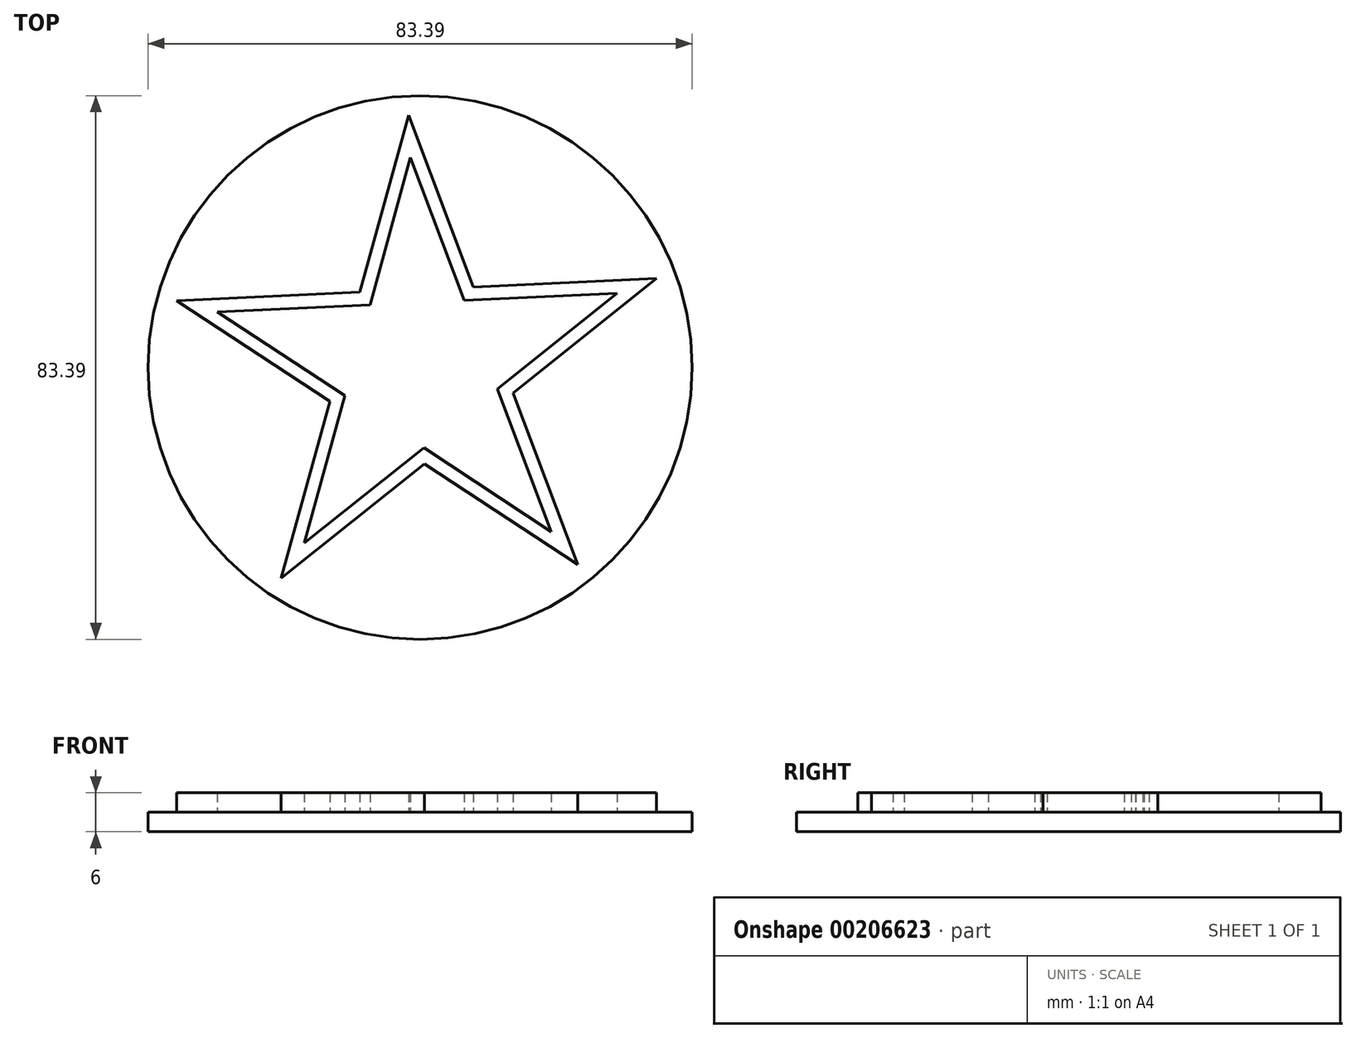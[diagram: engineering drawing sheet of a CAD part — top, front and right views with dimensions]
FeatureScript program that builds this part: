
annotation { "Feature Type Name" : "Feature", "Feature Type Description" : "" }
export const myFeature = defineFeature(function(context is Context, id is Id, definition is map)
    precondition{}
    {
        {
            var Q0;
            Q0=qCreatedBy(makeId("Top.planeOp"),FACE);
            var sketch = newSketch(context, id + "F0", { "sketchPlane" : qUnion([Q0])});
            skLineSegment(sketch, "E0", {"start": v(-46.48, 17.77) * mm, "end": v(-18.4, 19.06) * mm});
            skLineSegment(sketch, "E1", {"start": v(-18.4, 19.06) * mm, "end": v(-10.94, 46.17) * mm});
            skLineSegment(sketch, "E2", {"start": v(-10.94, 46.17) * mm, "end": v(-1.04, 19.86) * mm});
            skLineSegment(sketch, "E3", {"start": v(-1.04, 19.86) * mm, "end": v(27.05, 21.15) * mm});
            skLineSegment(sketch, "E4", {"start": v(27.05, 21.15) * mm, "end": v(5.08, 3.6) * mm});
            skLineSegment(sketch, "E5", {"start": v(5.08, 3.6) * mm, "end": v(15, -22.71) * mm});
            skLineSegment(sketch, "E6", {"start": v(15, -22.71) * mm, "end": v(-8.49, -7.25) * mm});
            skLineSegment(sketch, "E7", {"start": v(-8.49, -7.25) * mm, "end": v(-30.45, -24.8) * mm});
            skLineSegment(sketch, "E8", {"start": v(-30.45, -24.8) * mm, "end": v(-23, 2.3) * mm});
            skLineSegment(sketch, "E9", {"start": v(-23, 2.3) * mm, "end": v(-46.48, 17.77) * mm});
            skLineSegment(sketch, "E10.0", {"start": v(-7.39, -5.58) * mm, "end": v(-8.6, -4.78) * mm});
            skLineSegment(sketch, "E11.0", {"start": v(-21.07, 1.78) * mm, "end": v(-20.69, 3.18) * mm});
            skLineSegment(sketch, "E12.0", {"start": v(-0.95, 17.86) * mm, "end": v(20.99, 18.87) * mm});
            skLineSegment(sketch, "E13.0", {"start": v(3.21, 2.9) * mm, "end": v(10.95, -17.66) * mm});
            skLineSegment(sketch, "E14.0", {"start": v(-9.74, -5.69) * mm, "end": v(-26.9, -19.4) * mm});
            skLineSegment(sketch, "E15.trimOffspring", {"start": v(-10.65, 39.7) * mm, "end": v(-2.4, 17.8) * mm});
            skLineSegment(sketch, "E16.trimOffspring", {"start": v(20.99, 18.87) * mm, "end": v(2.7, 4.25) * mm});
            skLineSegment(sketch, "E17.trimOffspring", {"start": v(10.95, -17.66) * mm, "end": v(-7.39, -5.58) * mm});
            skLineSegment(sketch, "E18.trimOffspring", {"start": v(-26.9, -19.4) * mm, "end": v(-21.07, 1.78) * mm});
            skLineSegment(sketch, "E19.trimOffspring", {"start": v(-40.24, 16.06) * mm, "end": v(-16.85, 17.13) * mm});
            skLineSegment(sketch, "E20.trimOffspring", {"start": v(-2.4, 17.8) * mm, "end": v(-0.95, 17.86) * mm});
            skLineSegment(sketch, "E21.trimOffspring", {"start": v(2.7, 4.25) * mm, "end": v(3.21, 2.9) * mm});
            skLineSegment(sketch, "E22.trimOffspring", {"start": v(-8.6, -4.78) * mm, "end": v(-9.74, -5.69) * mm});
            skLineSegment(sketch, "E23.trimOffspring", {"start": v(-20.69, 3.18) * mm, "end": v(-40.24, 16.06) * mm});
            skLineSegment(sketch, "E24.trimOffspring", {"start": v(-16.85, 17.13) * mm, "end": v(-10.65, 39.7) * mm});
            skCircle(sketch, "E25.0", {"center": v(-9.17, 7.51) * mm, "radius": 41.7 * mm});
            skLineSegment(sketch, "E26.0", {"start": v(-17.43, 18.8) * mm, "end": v(-9.98, 45.9) * mm});
            skLineSegment(sketch, "E27.0", {"start": v(-1, 18.86) * mm, "end": v(27.1, 20.15) * mm});
            skSolve(sketch);
        }
        {
            var Q0;
            Q0=makeQuery(id+"F0.imprint","IMPRINT",FACE,{"disambiguationData":[TD([[makeQuery(id+"F0.imprint","IMPRINT",EDGE,{"derivedFrom":sQuery(id+"F0.wireOp",EDGE,"E0")}),-1.0]])]});
            extrude(context, id + "F1", {"entities" : qUnion([Q0]), "depth" : 6 * mm});
        }
        {
            var Q0;
            Q0=makeQuery(id+"F0.imprint","IMPRINT",FACE,{"disambiguationData":[TD([[makeQuery(id+"F0.imprint","IMPRINT",EDGE,{"derivedFrom":sQuery(id+"F0.wireOp",EDGE,"E0")}),1.0]])]});
            var Q1;
            Q1=makeQuery(id+"F0.imprint","IMPRINT",FACE,{"disambiguationData":[TD([[makeQuery(id+"F0.imprint","IMPRINT",EDGE,{"derivedFrom":sQuery(id+"F0.wireOp",EDGE,"E10.0")}),-1.0]])]});
            extrude(context, id + "F2", {"entities" : qUnion([Q0, Q1]), "operationType" : NewBodyOperationType.ADD, "depth" : 3 * mm});
        }
    });
